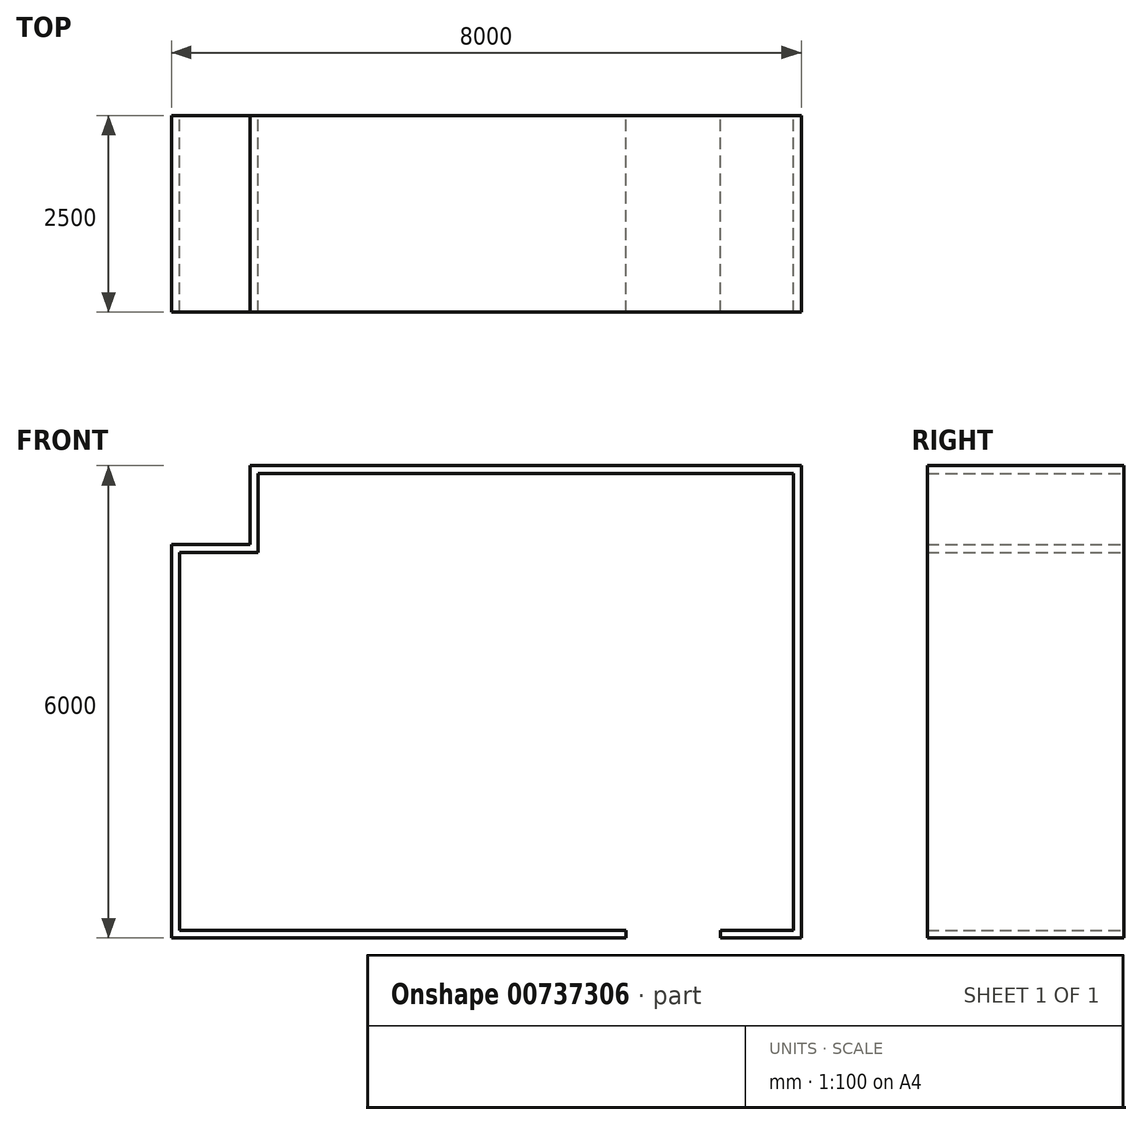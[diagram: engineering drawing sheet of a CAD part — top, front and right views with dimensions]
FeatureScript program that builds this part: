
annotation { "Feature Type Name" : "Feature", "Feature Type Description" : "" }
export const myFeature = defineFeature(function(context is Context, id is Id, definition is map)
    precondition{}
    {
        {
            var Q0;
            Q0=qCreatedBy(makeId("Front.planeOp"),FACE);
            var sketch = newSketch(context, id + "F0", { "sketchPlane" : qUnion([Q0])});
            skLineSegment(sketch, "E0", {"start": v(-551.35, -898.22) * mm, "end": v(448.65, -898.22) * mm});
            skLineSegment(sketch, "E1", {"start": v(448.65, -898.22) * mm, "end": v(448.65, 101.78) * mm});
            skLineSegment(sketch, "E2", {"start": v(448.65, 101.78) * mm, "end": v(7448.65, 101.78) * mm});
            skLineSegment(sketch, "E3", {"start": v(7448.65, 101.78) * mm, "end": v(7448.65, -5898.22) * mm});
            skLineSegment(sketch, "E4", {"start": v(7448.65, -5898.22) * mm, "end": v(6418.53, -5898.22) * mm});
            skLineSegment(sketch, "E5", {"start": v(6418.53, -5898.22) * mm, "end": v(6418.53, -5798.22) * mm});
            skLineSegment(sketch, "E6", {"start": v(6418.53, -5798.22) * mm, "end": v(7348.65, -5798.22) * mm});
            skLineSegment(sketch, "E7", {"start": v(7348.65, -5798.22) * mm, "end": v(7348.65, 1.78) * mm});
            skLineSegment(sketch, "E8", {"start": v(7348.65, 1.78) * mm, "end": v(548.65, 1.78) * mm});
            skLineSegment(sketch, "E9", {"start": v(548.65, 1.78) * mm, "end": v(548.65, -998.22) * mm});
            skLineSegment(sketch, "E10", {"start": v(548.65, -998.22) * mm, "end": v(-451.35, -998.22) * mm});
            skLineSegment(sketch, "E11", {"start": v(-451.35, -998.22) * mm, "end": v(-451.35, -5798.22) * mm});
            skLineSegment(sketch, "E12", {"start": v(-451.35, -5798.22) * mm, "end": v(5218.53, -5798.22) * mm});
            skLineSegment(sketch, "E13", {"start": v(5218.53, -5798.22) * mm, "end": v(5218.53, -5898.22) * mm});
            skLineSegment(sketch, "E14", {"start": v(5218.53, -5898.22) * mm, "end": v(-551.35, -5898.22) * mm});
            skLineSegment(sketch, "E15", {"start": v(-551.35, -5898.22) * mm, "end": v(-551.35, -898.22) * mm});
            skSolve(sketch);
        }
        {
            var Q0;
            Q0 = qSketchRegion(id + "F0", true);
            extrude(context, id + "F1", {"entities" : qUnion([Q0]), "depth" : 2500 * mm, "offsetDistance" : 25 * mm});
        }
    });
